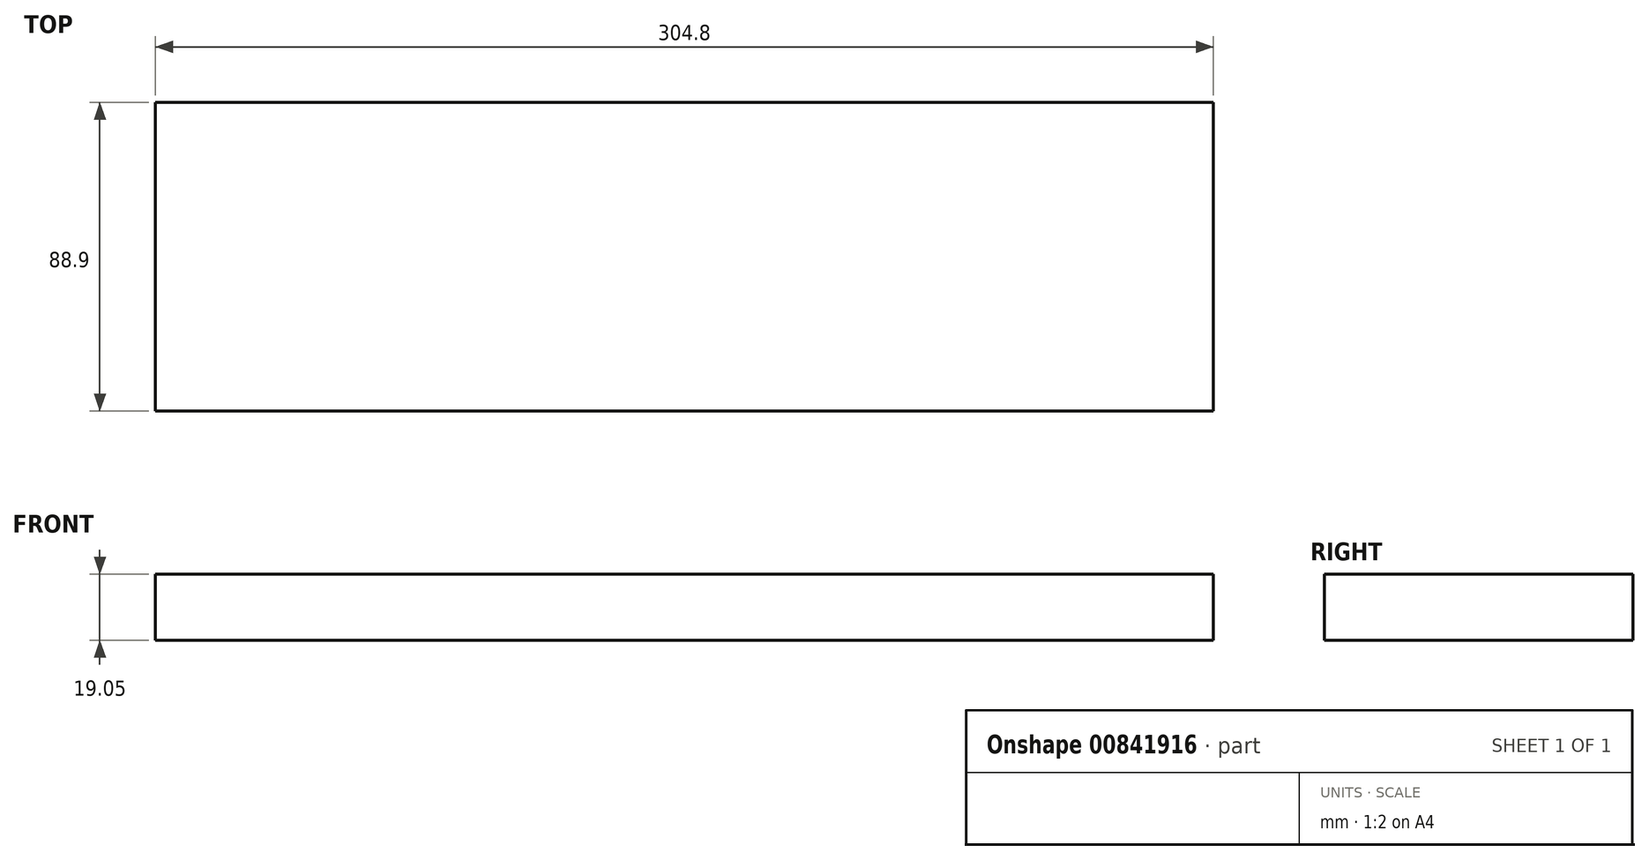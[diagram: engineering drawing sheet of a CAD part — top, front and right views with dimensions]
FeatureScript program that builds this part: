
annotation { "Feature Type Name" : "Feature", "Feature Type Description" : "" }
export const myFeature = defineFeature(function(context is Context, id is Id, definition is map)
    precondition{}
    {
        {
            var Q0;
            Q0=qCreatedBy(makeId("Right.planeOp"),FACE);
            var sketch = newSketch(context, id + "F0", { "sketchPlane" : qUnion([Q0])});
            skLineSegment(sketch, "E0.bottom", {"start": v(0, 0) * mm, "end": v(88.9, 0) * mm});
            skLineSegment(sketch, "E0.top", {"start": v(0, 19.05) * mm, "end": v(88.9, 19.05) * mm});
            skLineSegment(sketch, "E0.left", {"start": v(0, 0) * mm, "end": v(0, 19.05) * mm});
            skLineSegment(sketch, "E0.right", {"start": v(88.9, 0) * mm, "end": v(88.9, 19.05) * mm});
            skSolve(sketch);
        }
        {
            var Q0;
            Q0 = qSketchRegion(id + "F0", true);
            extrude(context, id + "F1", {"entities" : qUnion([Q0]), "depth" : 304.8 * mm, "offsetDistance" : 25.4 * mm});
        }
    });
